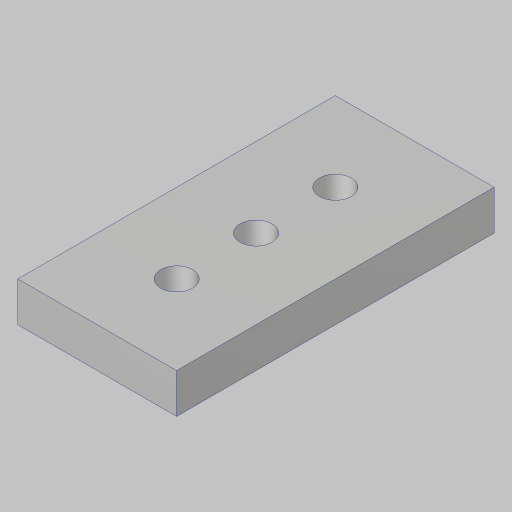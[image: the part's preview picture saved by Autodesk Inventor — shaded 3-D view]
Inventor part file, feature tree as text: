
AUTODESK INVENTOR PART (.ipt)
format: ipt  version: 2023.5 (Build 275446000, 446)  size: 96,256 bytes
history: native  units: in
note: dims shown in document units (in); Inventor stores cm internally (conversion verified against a paired STEP export)
features: sketch x2, extrude x1, hole x1
ambient origin geometry x8: Origin, YZ Plane, XZ Plane, XY Plane, X Axis, Y Axis, Z Axis, Center Point
bodies: Solid1 (feature_tree)
feature tree (4):
  extrude  "Extrusion1"  Depth=2.0in
  hole  "Hole1"  [1 undecoded]
  sketch  "Sketch2"  dims[d0=1.0in d1=2.0in]
  sketch  "Sketch3"  dims[d2=0.25in d3=0.0in d4=0.5in d5=0.5in d6=0.201in d7=0.75in d8=0.385in d9=0.25in d10=0.5635in d11=1.0in d12=0.8108in]
note: 1 required parameter value undecoded (feature->parameter linkage not recoverable at this tier; creation-order binding heuristic only, values carry confidence <= 0.55)
